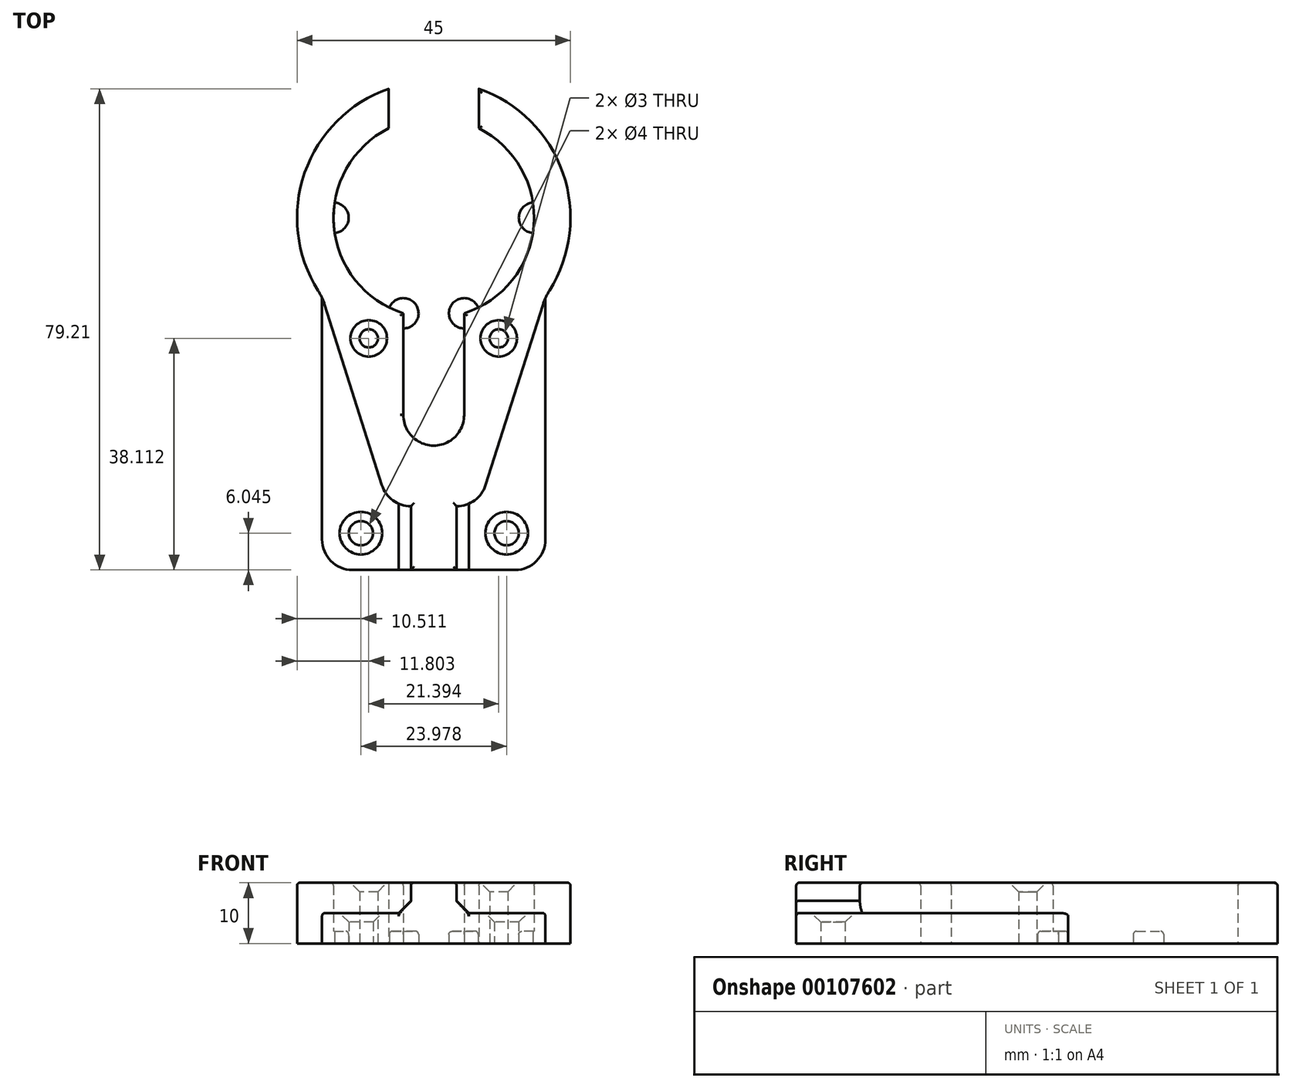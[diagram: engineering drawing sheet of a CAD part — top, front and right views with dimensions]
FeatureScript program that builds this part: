
annotation { "Feature Type Name" : "Feature", "Feature Type Description" : "" }
export const myFeature = defineFeature(function(context is Context, id is Id, definition is map)
    precondition{}
    {
        {
            var Q0;
            Q0=qCreatedBy(makeId("Top.planeOp"),FACE);
            var sketch = newSketch(context, id + "F0", { "sketchPlane" : qUnion([Q0])});
            skArc(sketch, "E0", {"start": v(-7.43, 14.73) * mm, "mid": v(-16.45, -1.31) * mm, "end": v(-5, -15.72) * mm});
            skArc(sketch, "E1", {"start": v(-7.43, 21.24) * mm, "mid": v(-21.24, 7.42) * mm, "end": v(-19.03, -12) * mm});
            skLineSegment(sketch, "E2.top", {"start": v(-3.77, -47.5) * mm, "end": v(3.77, -47.5) * mm});
            skLineSegment(sketch, "E2.left", {"start": v(-7.43, 21.24) * mm, "end": v(-7.43, 14.73) * mm});
            skLineSegment(sketch, "E2.right", {"start": v(7.43, 21.24) * mm, "end": v(7.43, 14.73) * mm});
            skArc(sketch, "E3", {"start": v(-16.31, -2.5) * mm, "mid": v(-14, 0) * mm, "end": v(-16.31, 2.5) * mm});
            skArc(sketch, "E4", {"start": v(16.31, 2.5) * mm, "mid": v(14, 0) * mm, "end": v(16.31, -2.5) * mm});
            skArc(sketch, "E5", {"start": v(-5, -32.45) * mm, "mid": v(-0.03, -37.5) * mm, "end": v(5, -32.5) * mm});
            skLineSegment(sketch, "E6", {"start": v(-5, -32.45) * mm, "end": v(-5, -15.72) * mm});
            skLineSegment(sketch, "E7", {"start": v(5, -32.5) * mm, "end": v(5, -15.72) * mm});
            skPoint(sketch, "E2.bottom.start.orphan", {"position": v(-7.43, 47.5) * mm});
            skPoint(sketch, "E8.orphan", {"position": v(7.43, 47.5) * mm});
            skArc(sketch, "E9.trimOffspring", {"start": v(5, -15.72) * mm, "mid": v(16.45, -1.31) * mm, "end": v(7.43, 14.73) * mm});
            skArc(sketch, "E10.trimOffspring", {"start": v(19.03, -12) * mm, "mid": v(21.24, 7.42) * mm, "end": v(7.43, 21.24) * mm});
            skLineSegment(sketch, "E11", {"start": v(-17.96, -14.31) * mm, "end": v(-8.53, -44.01) * mm});
            skLineSegment(sketch, "E12", {"start": v(17.96, -14.31) * mm, "end": v(8.53, -44.01) * mm});
            skPoint(sketch, "E13.orphan", {"position": v(-22.5, 0) * mm});
            skPoint(sketch, "E14.orphan", {"position": v(22.5, 0) * mm});
            skPoint(sketch, "E15.visualSharp", {"position": v(-7.43, -47.5) * mm});
            skArc(sketch, "E15.filletArc", {"start": v(-8.53, -44.01) * mm, "mid": v(-6.72, -46.53) * mm, "end": v(-3.77, -47.5) * mm});
            skPoint(sketch, "E16.visualSharp", {"position": v(7.43, -47.5) * mm});
            skArc(sketch, "E16.filletArc", {"start": v(3.77, -47.5) * mm, "mid": v(6.72, -46.53) * mm, "end": v(8.53, -44.01) * mm});
            skPoint(sketch, "E17.visualSharp", {"position": v(-18.38, -12.97) * mm});
            skArc(sketch, "E17.filletArc", {"start": v(-17.96, -14.31) * mm, "mid": v(-18.42, -13.12) * mm, "end": v(-19.03, -12) * mm});
            skPoint(sketch, "E18.visualSharp", {"position": v(18.38, -12.97) * mm});
            skArc(sketch, "E18.filletArc", {"start": v(19.03, -12) * mm, "mid": v(18.42, -13.12) * mm, "end": v(17.96, -14.31) * mm});
            skArc(sketch, "E19", {"start": v(-5, -18.22) * mm, "mid": v(-2.93, -14.33) * mm, "end": v(-7.32, -14.79) * mm});
            skArc(sketch, "E20", {"start": v(7.32, -14.79) * mm, "mid": v(2.93, -14.33) * mm, "end": v(5, -18.22) * mm});
            skPoint(sketch, "E21", {"position": v(0, -37.5) * mm});
            skCircle(sketch, "E22", {"center": v(-10.7, -19.86) * mm, "radius": 1.5 * mm});
            skLineSegment(sketch, "E23", {"start": v(0, 0) * mm, "end": v(0, -32.5) * mm, "construction": true});
            skCircle(sketch, "E24.MirrorC", {"center": v(10.7, -19.86) * mm, "radius": 1.5 * mm});
            skLineSegment(sketch, "E25", {"start": v(18.38, -12.97) * mm, "end": v(18.38, -52.97) * mm});
            skLineSegment(sketch, "E26", {"start": v(-18.38, -12.97) * mm, "end": v(-18.38, -52.97) * mm});
            skLineSegment(sketch, "E27", {"start": v(-13.38, -57.97) * mm, "end": v(13.38, -57.97) * mm});
            skLineSegment(sketch, "E28", {"start": v(3.77, -47.5) * mm, "end": v(3.77, -57.97) * mm});
            skLineSegment(sketch, "E29", {"start": v(-3.77, -47.5) * mm, "end": v(-3.77, -57.97) * mm});
            skCircle(sketch, "E30", {"center": v(11.99, -51.93) * mm, "radius": 2 * mm});
            skCircle(sketch, "E31.MirrorC", {"center": v(-11.99, -51.93) * mm, "radius": 2 * mm});
            skPoint(sketch, "E32.visualSharp", {"position": v(18.38, -57.97) * mm});
            skArc(sketch, "E32.filletArc", {"start": v(13.38, -57.97) * mm, "mid": v(16.92, -56.5) * mm, "end": v(18.38, -52.97) * mm});
            skPoint(sketch, "E33.visualSharp", {"position": v(-18.38, -57.97) * mm});
            skArc(sketch, "E33.filletArc", {"start": v(-18.38, -52.97) * mm, "mid": v(-16.92, -56.5) * mm, "end": v(-13.38, -57.97) * mm});
            skSolve(sketch);
        }
        {
            var Q0;
            Q0=makeQuery(id+"F0.imprint","IMPRINT",FACE,{"disambiguationData":[TD([[makeQuery(id+"F0.imprint","IMPRINT",EDGE,{"derivedFrom":sQuery(id+"F0.wireOp",EDGE,"E1")}),1.0]])]});
            extrude(context, id + "F1", {"entities" : qUnion([Q0]), "depth" : 10 * mm});
        }
        {
            var Q0;
            {var subQ0=sQuery(id+"F0.wireOp",EDGE,"E3");Q0=makeQuery(id+"F0.imprint","IMPRINT",FACE,{"disambiguationData":[TD([[makeQuery(id+"F0.imprint","IMPRINT",EDGE,{"derivedFrom":subQ0}),1.0]])]});}
            var Q1;
            {var subQ0=sQuery(id+"F0.wireOp",EDGE,"E4");Q1=makeQuery(id+"F0.imprint","IMPRINT",FACE,{"disambiguationData":[TD([[makeQuery(id+"F0.imprint","IMPRINT",EDGE,{"derivedFrom":subQ0}),1.0]])]});}
            var Q2;
            {var subQ3=sQuery(id+"F0.wireOp",EDGE,"E19");Q2=makeQuery(id+"F0.imprint","IMPRINT",FACE,{"disambiguationData":[TD([[makeQuery(id+"F0.imprint","IMPRINT",EDGE,{"derivedFrom":subQ3}),1.0]])]});}
            var Q3;
            {var subQ3=sQuery(id+"F0.wireOp",EDGE,"E20");Q3=makeQuery(id+"F0.imprint","IMPRINT",FACE,{"disambiguationData":[TD([[makeQuery(id+"F0.imprint","IMPRINT",EDGE,{"derivedFrom":subQ3}),1.0]])]});}
            extrude(context, id + "F2", {"entities" : qUnion([Q0, Q1, Q2, Q3]), "operationType" : NewBodyOperationType.ADD, "depth" : 2 * mm});
        }
        {
            var Q0;
            {var subQ4=sQuery(id+"F0.wireOp",EDGE,"E11");Q0=makeQuery(id+"F0.imprint","IMPRINT",FACE,{"disambiguationData":[TD([[makeQuery(id+"F0.imprint","IMPRINT",EDGE,{"derivedFrom":subQ4}),-1.0]])]});}
            var Q1;
            Q1=makeQuery(id+"F0.imprint","IMPRINT",FACE,{"disambiguationData":[TD([[makeQuery(id+"F0.imprint","IMPRINT",EDGE,{"derivedFrom":sQuery(id+"F0.wireOp",EDGE,"E2.top")}),-1.0]])]});
            var Q2;
            {var subQ1=sQuery(id+"F0.wireOp",EDGE,"E12");Q2=makeQuery(id+"F0.imprint","IMPRINT",FACE,{"disambiguationData":[TD([[makeQuery(id+"F0.imprint","IMPRINT",EDGE,{"derivedFrom":subQ1}),1.0]])]});}
            extrude(context, id + "F3", {"entities" : qUnion([Q0, Q1, Q2]), "operationType" : NewBodyOperationType.ADD, "depth" : 5 * mm});
        }
        {
            var Q0;
            Q0=makeQuery(id+"F1.opExtrude","CAP_EDGE",EDGE,{"disambiguationData":[OSD([sQuery(id+"F0.wireOp",EDGE,"E22")])],"isStart":false});
            var Q1;
            Q1=makeQuery(id+"F1.opExtrude","CAP_EDGE",EDGE,{"disambiguationData":[OSD([sQuery(id+"F0.wireOp",EDGE,"E24.MirrorC")])],"isStart":false});
            var Q2;
            Q2=makeQuery(id+"F3.opExtrude","CAP_EDGE",EDGE,{"disambiguationData":[OSD([sQuery(id+"F0.wireOp",EDGE,"E30")])],"isStart":false});
            var Q3;
            Q3=makeQuery(id+"F3.opExtrude","CAP_EDGE",EDGE,{"disambiguationData":[OSD([sQuery(id+"F0.wireOp",EDGE,"E31.MirrorC")])],"isStart":false});
            chamfer(context, id + "F4", {"entities" : qUnion([Q0, Q1, Q2, Q3]), "width" : 1.5 * mm, "tangentPropagation" : true});
        }
        {
            var Q0;
            Q0=makeQuery(id+"F0.imprint","IMPRINT",FACE,{"disambiguationData":[TD([[makeQuery(id+"F0.imprint","IMPRINT",EDGE,{"derivedFrom":sQuery(id+"F0.wireOp",EDGE,"E2.top")}),-1.0]])]});
            extrude(context, id + "F5", {"entities" : qUnion([Q0]), "operationType" : NewBodyOperationType.ADD, "depth" : 10 * mm});
        }
        {
            var Q0;
            Q0=makeQuery(id+"F1.opExtrude","CAP_EDGE",EDGE,{"disambiguationData":[OSD([sQuery(id+"F0.wireOp",EDGE,"E1")])],"isStart":false});
            var Q1;
            Q1=makeQuery(id+"F1.opExtrude","CAP_EDGE",EDGE,{"disambiguationData":[OSD([sQuery(id+"F0.wireOp",EDGE,"E6")])],"isStart":false});
            var Q2;
            Q2=makeQuery(id+"F1.opExtrude","CAP_EDGE",EDGE,{"disambiguationData":[OSD([sQuery(id+"F0.wireOp",EDGE,"E7")])],"isStart":false});
            var Q3;
            Q3=makeQuery(id+"F2.opExtrude","CAP_EDGE",EDGE,{"disambiguationData":[OSD([sQuery(id+"F0.wireOp",EDGE,"E3")])],"isStart":false});
            var Q4;
            Q4=makeQuery(id+"F2.opExtrude","CAP_EDGE",EDGE,{"disambiguationData":[OSD([sQuery(id+"F0.wireOp",EDGE,"E4")])],"isStart":false});
            var Q5;
            Q5=makeQuery(id+"F1.opExtrude","CAP_EDGE",EDGE,{"disambiguationData":[OSD([sQuery(id+"F0.wireOp",EDGE,"E2.left")])],"isStart":false});
            var Q6;
            Q6=makeQuery(id+"F1.opExtrude","CAP_EDGE",EDGE,{"disambiguationData":[OSD([sQuery(id+"F0.wireOp",EDGE,"E2.right")])],"isStart":false});
            var Q7;
            Q7=makeQuery(id+"F2.opExtrude","CAP_EDGE",EDGE,{"disambiguationData":[OSD([sQuery(id+"F0.wireOp",EDGE,"E19")])],"isStart":false});
            var Q8;
            Q8=makeQuery(id+"F2.opExtrude","CAP_EDGE",EDGE,{"disambiguationData":[OSD([sQuery(id+"F0.wireOp",EDGE,"E20")])],"isStart":false});
            var Q9;
            Q9=makeQuery(id+"F1.opExtrude","CAP_EDGE",EDGE,{"disambiguationData":[OSD([sQuery(id+"F0.wireOp",EDGE,"E0")])],"isStart":false});
            var Q10;
            Q10=makeQuery(id+"F1.opExtrude","CAP_EDGE",EDGE,{"disambiguationData":[OSD([sQuery(id+"F0.wireOp",EDGE,"E9.trimOffspring")])],"isStart":false});
            var Q11;
            Q11=makeQuery(id+"F1.opExtrude","CAP_EDGE",EDGE,{"disambiguationData":[OSD([sQuery(id+"F0.wireOp",EDGE,"E10.trimOffspring")])],"isStart":false});
            var Q12;
            Q12=makeQuery(id+"F3.opExtrude","CAP_EDGE",EDGE,{"disambiguationData":[OSD([sQuery(id+"F0.wireOp",EDGE,"E25")])],"isStart":false});
            var Q13;
            Q13=makeQuery(id+"F3.opExtrude","CAP_EDGE",EDGE,{"disambiguationData":[OSD([sQuery(id+"F0.wireOp",EDGE,"E26")])],"isStart":false});
            var Q14;
            Q14=makeQuery(id+"F5.opExtrude","CAP_EDGE",EDGE,{"disambiguationData":[OSD([sQuery(id+"F0.wireOp",EDGE,"E29")])],"isStart":false});
            var Q15;
            Q15=makeQuery(id+"F5.opExtrude","CAP_EDGE",EDGE,{"disambiguationData":[OSD([sQuery(id+"F0.wireOp",EDGE,"E27")])],"isStart":false});
            var Q16;
            Q16=makeQuery(id+"F5.opExtrude","CAP_EDGE",EDGE,{"disambiguationData":[OSD([sQuery(id+"F0.wireOp",EDGE,"E28")])],"isStart":false});
            fillet(context, id + "F6", {"entities" : qUnion([Q0, Q1, Q2, Q3, Q4, Q5, Q6, Q7, Q8, Q9, Q10, Q11, Q12, Q13, Q14, Q15, Q16]), "radius" : 0.5 * mm, "tangentPropagation" : true, "allowEdgeOverflow" : false});
        }
        {
            var Q0;
            Q0=makeQuery(id+"F5.boolean.opBoolean","INTERSECT",EDGE,{"derivedFrom":[makeQuery(id+"F3.opExtrude","CAP_FACE",FACE,{"disambiguationData":[OSD([sQuery(id+"F0.wireOp",EDGE,"E2.top"),sQuery(id+"F0.wireOp",EDGE,"E11"),sQuery(id+"F0.wireOp",EDGE,"E12"),sQuery(id+"F0.wireOp",EDGE,"E15.filletArc"),sQuery(id+"F0.wireOp",EDGE,"E16.filletArc"),sQuery(id+"F0.wireOp",EDGE,"E17.filletArc"),sQuery(id+"F0.wireOp",EDGE,"E18.filletArc"),sQuery(id+"F0.wireOp",EDGE,"E25"),sQuery(id+"F0.wireOp",EDGE,"E26"),sQuery(id+"F0.wireOp",EDGE,"E27"),sQuery(id+"F0.wireOp",EDGE,"E30"),sQuery(id+"F0.wireOp",EDGE,"E31.MirrorC"),sQuery(id+"F0.wireOp",EDGE,"E32.filletArc"),sQuery(id+"F0.wireOp",EDGE,"E33.filletArc")])],"isStart":false}),makeQuery(id+"F5.opExtrude","SWEPT_FACE",FACE,{"disambiguationData":[OSD([sQuery(id+"F0.wireOp",EDGE,"E28")])]})]});
            var Q1;
            Q1=makeQuery(id+"F5.boolean.opBoolean","INTERSECT",EDGE,{"derivedFrom":[makeQuery(id+"F3.opExtrude","CAP_FACE",FACE,{"disambiguationData":[OSD([sQuery(id+"F0.wireOp",EDGE,"E2.top"),sQuery(id+"F0.wireOp",EDGE,"E11"),sQuery(id+"F0.wireOp",EDGE,"E12"),sQuery(id+"F0.wireOp",EDGE,"E15.filletArc"),sQuery(id+"F0.wireOp",EDGE,"E16.filletArc"),sQuery(id+"F0.wireOp",EDGE,"E17.filletArc"),sQuery(id+"F0.wireOp",EDGE,"E18.filletArc"),sQuery(id+"F0.wireOp",EDGE,"E25"),sQuery(id+"F0.wireOp",EDGE,"E26"),sQuery(id+"F0.wireOp",EDGE,"E27"),sQuery(id+"F0.wireOp",EDGE,"E30"),sQuery(id+"F0.wireOp",EDGE,"E31.MirrorC"),sQuery(id+"F0.wireOp",EDGE,"E32.filletArc"),sQuery(id+"F0.wireOp",EDGE,"E33.filletArc")])],"isStart":false}),makeQuery(id+"F5.opExtrude","SWEPT_FACE",FACE,{"disambiguationData":[OSD([sQuery(id+"F0.wireOp",EDGE,"E29")])]})]});
            var Q2;
            Q2=makeQuery(id+"F3.opExtrude","CAP_EDGE",EDGE,{"disambiguationData":[OSD([sQuery(id+"F0.wireOp",EDGE,"E15.filletArc")])],"isStart":false});
            var Q3;
            Q3=makeQuery(id+"F3.opExtrude","CAP_EDGE",EDGE,{"disambiguationData":[OSD([sQuery(id+"F0.wireOp",EDGE,"E16.filletArc")])],"isStart":false});
            chamfer(context, id + "F7", {"entities" : qUnion([Q0, Q1, Q2, Q3]), "width" : 2 * mm, "tangentPropagation" : true});
        }
    });
